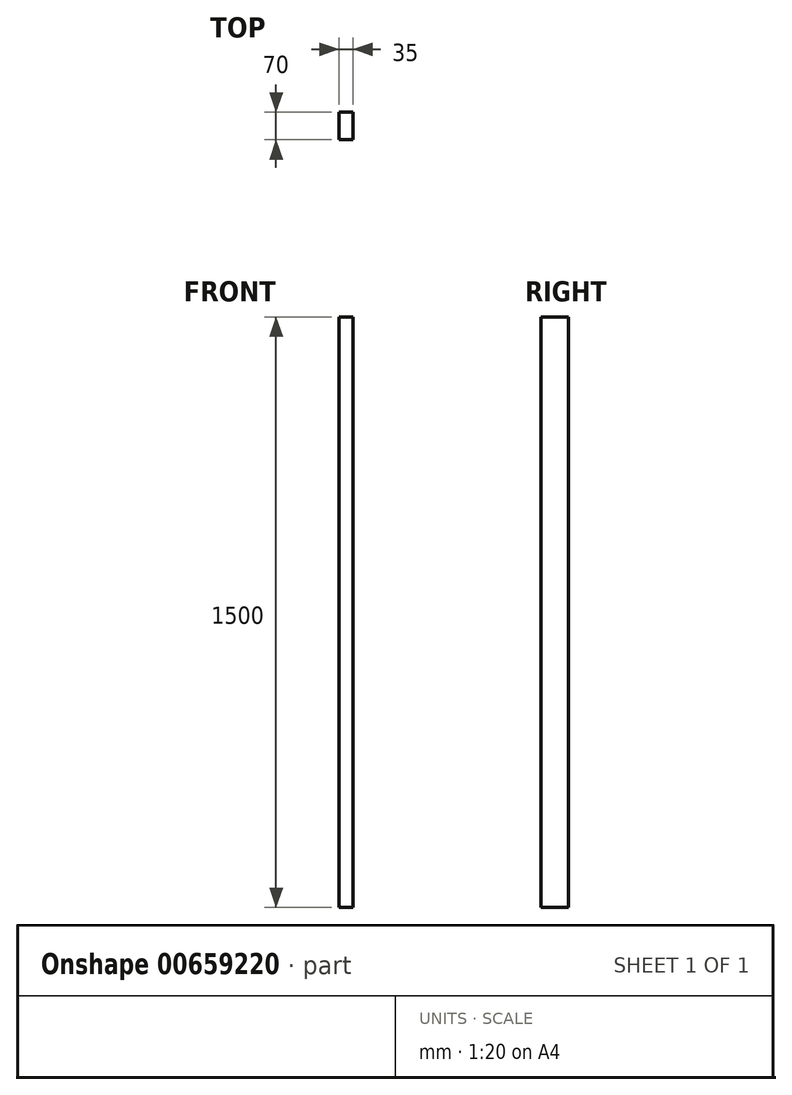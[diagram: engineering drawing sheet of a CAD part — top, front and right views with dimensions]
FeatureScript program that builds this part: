
annotation { "Feature Type Name" : "Feature", "Feature Type Description" : "" }
export const myFeature = defineFeature(function(context is Context, id is Id, definition is map)
    precondition{}
    {
        {
            var Q0;
            Q0=qCreatedBy(makeId("Top.planeOp"),FACE);
            var sketch = newSketch(context, id + "F0", { "sketchPlane" : qUnion([Q0])});
            skLineSegment(sketch, "E0.bottom", {"start": v(-17.5, 35) * mm, "end": v(17.5, 35) * mm});
            skLineSegment(sketch, "E0.top", {"start": v(-17.5, -35) * mm, "end": v(17.5, -35) * mm});
            skLineSegment(sketch, "E0.left", {"start": v(-17.5, 35) * mm, "end": v(-17.5, -35) * mm});
            skLineSegment(sketch, "E0.right", {"start": v(17.5, 35) * mm, "end": v(17.5, -35) * mm});
            skLineSegment(sketch, "E1", {"start": v(0, 0) * mm, "end": v(17.5, 0) * mm, "construction": true});
            skLineSegment(sketch, "E2", {"start": v(0, 0) * mm, "end": v(0, 35) * mm, "construction": true});
            skSolve(sketch);
        }
        {
            var Q0;
            Q0=makeQuery(id+"F0.imprint","IMPRINT",FACE,{"disambiguationData":[TD([[makeQuery(id+"F0.imprint","IMPRINT",EDGE,{"derivedFrom":sQuery(id+"F0.wireOp",EDGE,"E0.bottom")}),-1.0]])]});
            extrude(context, id + "F1", {"entities" : qUnion([Q0]), "depth" : 750 * mm, "offsetDistance" : 25 * mm, "hasSecondDirection" : true, "secondDirectionOppositeDirection" : true, "secondDirectionDepth" : 750 * mm});
        }
    });
